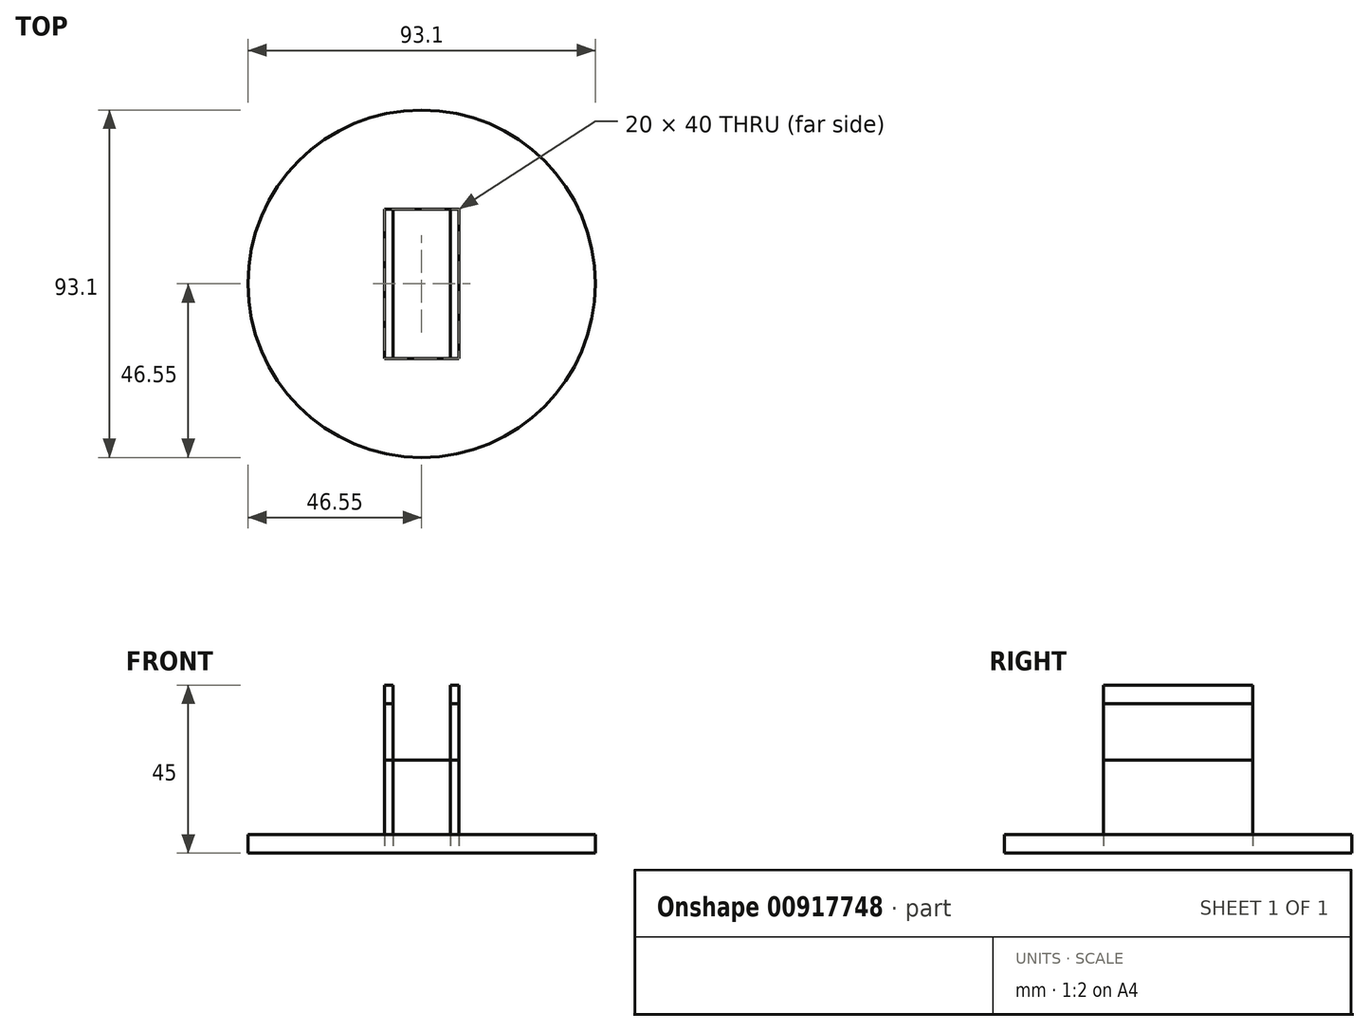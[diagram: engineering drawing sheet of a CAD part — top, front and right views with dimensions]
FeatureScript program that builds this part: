
annotation { "Feature Type Name" : "Feature", "Feature Type Description" : "" }
export const myFeature = defineFeature(function(context is Context, id is Id, definition is map)
    precondition{}
    {
        {
            var Q0;
            Q0=qCreatedBy(makeId("Top.planeOp"),FACE);
            var sketch = newSketch(context, id + "F0", { "sketchPlane" : qUnion([Q0])});
            skLineSegment(sketch, "E0.bottom", {"start": v(7.68, -20) * mm, "end": v(-7.67, -20) * mm});
            skLineSegment(sketch, "E0.top", {"start": v(7.68, 20) * mm, "end": v(-7.67, 20) * mm});
            skLineSegment(sketch, "E0.left", {"start": v(7.68, -20) * mm, "end": v(7.68, 20) * mm});
            skLineSegment(sketch, "E0.right", {"start": v(-7.67, -20) * mm, "end": v(-7.67, 20) * mm});
            skPoint(sketch, "E0.middle", {"position": v(0, 0) * mm});
            skLineSegment(sketch, "E1.bottom", {"start": v(-10, -20) * mm, "end": v(10, -20) * mm});
            skLineSegment(sketch, "E1.top", {"start": v(-10, 20) * mm, "end": v(10, 20) * mm});
            skLineSegment(sketch, "E1.left", {"start": v(-10, -20) * mm, "end": v(-10, 20) * mm});
            skLineSegment(sketch, "E1.right", {"start": v(10, -20) * mm, "end": v(10, 20) * mm});
            skCircle(sketch, "E2", {"center": v(0, 0) * mm, "radius": 46.55 * mm});
            skSolve(sketch);
        }
        {
            var Q0;
            Q0 = qSketchRegion(id + "F0", true);
            extrude(context, id + "F1", {"entities" : qUnion([Q0]), "depth" : 5 * mm, "offsetDistance" : 25 * mm});
        }
        {
            var Q0;
            {var subQ0=sQuery(id+"F0.wireOp",EDGE,"E0.right");Q0=makeQuery(id+"F0.imprint","IMPRINT",FACE,{"disambiguationData":[TD([[makeQuery(id+"F0.imprint","IMPRINT",EDGE,{"derivedFrom":subQ0}),1.0]])]});}
            var Q1;
            {var subQ0=sQuery(id+"F0.wireOp",EDGE,"E0.left");Q1=makeQuery(id+"F0.imprint","IMPRINT",FACE,{"disambiguationData":[TD([[makeQuery(id+"F0.imprint","IMPRINT",EDGE,{"derivedFrom":subQ0}),-1.0]])]});}
            extrude(context, id + "F2", {"entities" : qUnion([Q0, Q1]), "depth" : 40 * mm, "offsetDistance" : 25 * mm});
        }
        {
            var Q0;
            Q0=qCreatedBy(makeId("Top.planeOp"),FACE);
            var sketch = newSketch(context, id + "F3", { "sketchPlane" : qUnion([Q0])});
            skLineSegment(sketch, "E3.bottom", {"start": v(10, 20) * mm, "end": v(-10, 20) * mm});
            skLineSegment(sketch, "E3.top", {"start": v(10, -20) * mm, "end": v(-10, -20) * mm});
            skLineSegment(sketch, "E3.left", {"start": v(10, 20) * mm, "end": v(10, -20) * mm});
            skLineSegment(sketch, "E3.right", {"start": v(-10, 20) * mm, "end": v(-10, -20) * mm});
            skPoint(sketch, "E3.middle", {"position": v(0, 0) * mm});
            skSolve(sketch);
        }
        {
            var Q0;
            Q0 = qSketchRegion(id + "F3", true);
            extrude(context, id + "F4", {"entities" : qUnion([Q0]), "depth" : 25 * mm, "offsetDistance" : 25 * mm});
        }
        {
            var Q0;
            Q0=makeQuery(id+"F2.opExtrude","CAP_FACE",FACE,{"disambiguationData":[OSD([sQuery(id+"F0.wireOp",EDGE,"E0.right"),sQuery(id+"F0.wireOp",EDGE,"E1.bottom"),sQuery(id+"F0.wireOp",EDGE,"E1.top"),sQuery(id+"F0.wireOp",EDGE,"E1.left")])],"isStart":false});
            var Q1;
            Q1=makeQuery(id+"F2.opExtrude","CAP_FACE",FACE,{"disambiguationData":[OSD([sQuery(id+"F0.wireOp",EDGE,"E0.left"),sQuery(id+"F0.wireOp",EDGE,"E1.bottom"),sQuery(id+"F0.wireOp",EDGE,"E1.top"),sQuery(id+"F0.wireOp",EDGE,"E1.right")])],"isStart":false});
            extrude(context, id + "F5", {"entities" : qUnion([Q0, Q1]), "depth" : 5 * mm, "offsetDistance" : 25 * mm});
        }
    });
